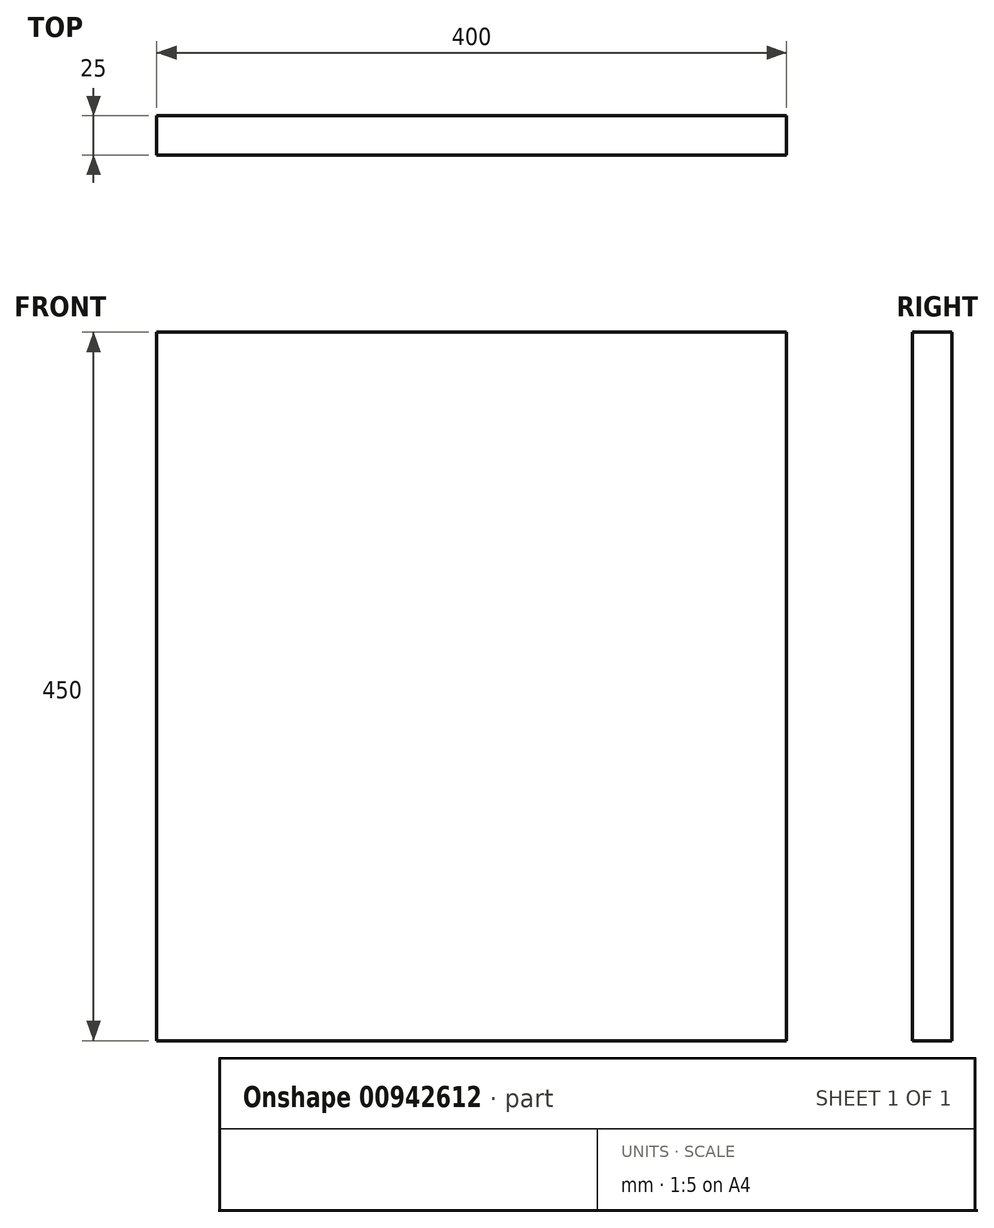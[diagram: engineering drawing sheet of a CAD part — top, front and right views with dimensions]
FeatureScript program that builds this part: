
annotation { "Feature Type Name" : "Feature", "Feature Type Description" : "" }
export const myFeature = defineFeature(function(context is Context, id is Id, definition is map)
    precondition{}
    {
        {
            var Q0;
            Q0=qCreatedBy(makeId("Front.planeOp"),FACE);
            var sketch = newSketch(context, id + "F0", { "sketchPlane" : qUnion([Q0])});
            skLineSegment(sketch, "E0.bottom", {"start": v(-200, 225) * mm, "end": v(200, 225) * mm});
            skLineSegment(sketch, "E0.top", {"start": v(-200, -225) * mm, "end": v(200, -225) * mm});
            skLineSegment(sketch, "E0.left", {"start": v(-200, 225) * mm, "end": v(-200, -225) * mm});
            skLineSegment(sketch, "E0.right", {"start": v(200, 225) * mm, "end": v(200, -225) * mm});
            skLineSegment(sketch, "E1", {"start": v(0, 239.72) * mm, "end": v(0, -204.54) * mm, "construction": true});
            skLineSegment(sketch, "E2", {"start": v(-236.88, 0) * mm, "end": v(248.23, 0) * mm, "construction": true});
            skSolve(sketch);
        }
        {
            var Q0;
            Q0 = qSketchRegion(id + "F0", true);
            extrude(context, id + "F1", {"entities" : qUnion([Q0]), "depth" : 25 * mm, "offsetDistance" : 25 * mm});
        }
    });
